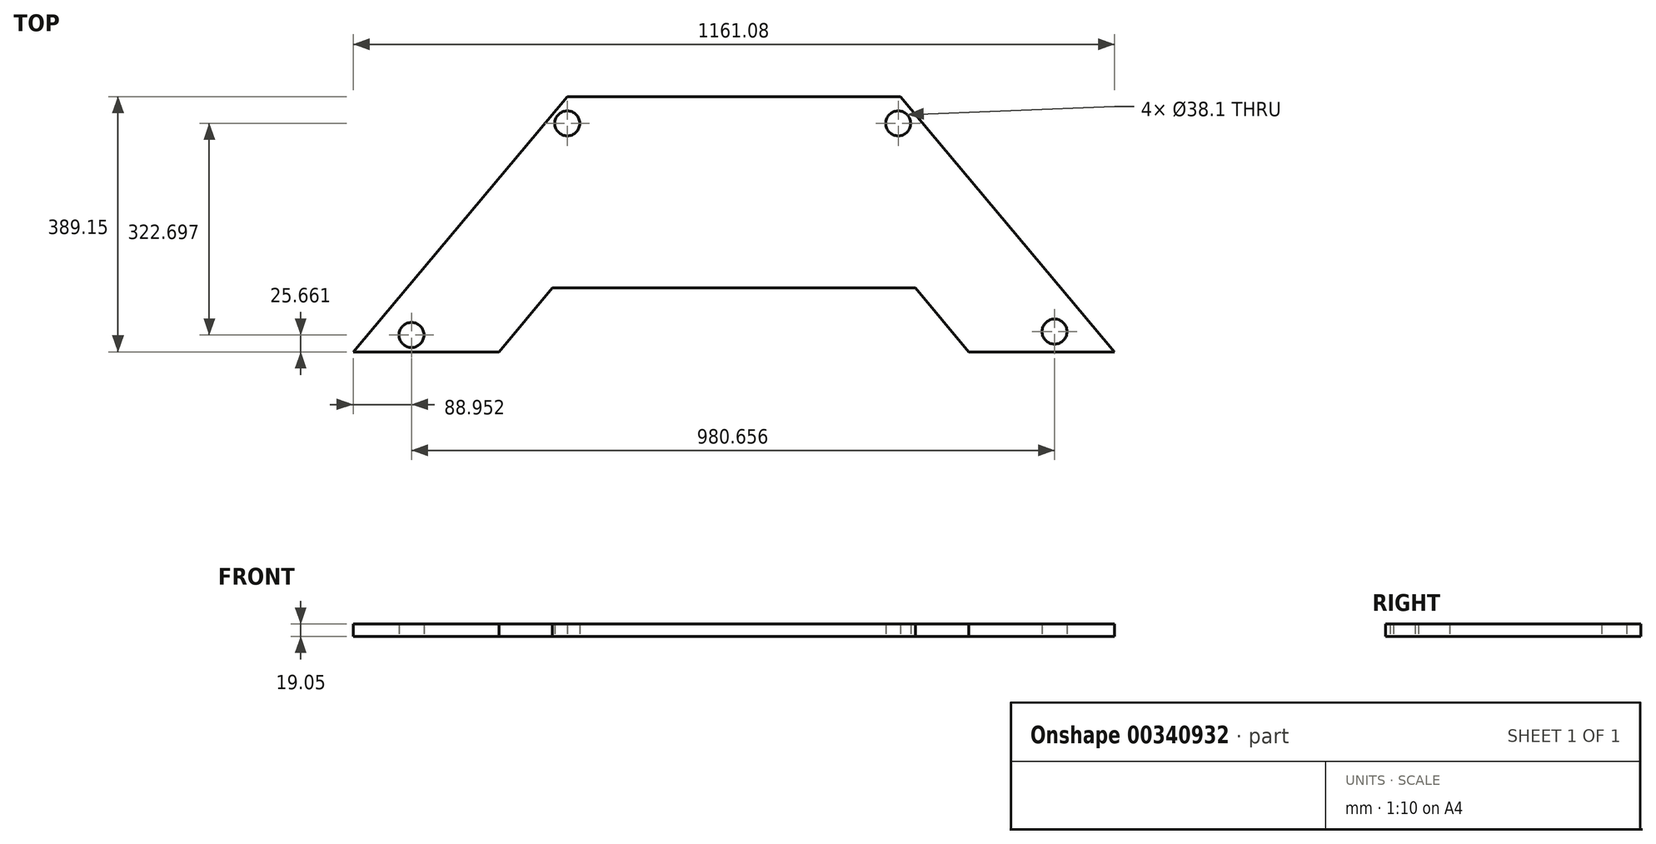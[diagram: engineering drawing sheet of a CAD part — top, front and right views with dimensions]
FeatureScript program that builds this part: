
annotation { "Feature Type Name" : "Feature", "Feature Type Description" : "" }
export const myFeature = defineFeature(function(context is Context, id is Id, definition is map)
    precondition{}
    {
        {
            var Q0;
            Q0=qCreatedBy(makeId("Top.planeOp"),FACE);
            var sketch = newSketch(context, id + "F0", { "sketchPlane" : qUnion([Q0])});
            skLineSegment(sketch, "E0", {"start": v(253.1, 0) * mm, "end": v(-254.9, 0) * mm});
            skLineSegment(sketch, "E1", {"start": v(-254.9, 0) * mm, "end": v(-581.43, -389.15) * mm});
            skLineSegment(sketch, "E2", {"start": v(253.1, 0) * mm, "end": v(579.65, -389.15) * mm});
            skLineSegment(sketch, "E3", {"start": v(-581.43, -389.15) * mm, "end": v(-359.18, -389.15) * mm});
            skLineSegment(sketch, "E4", {"start": v(579.65, -389.15) * mm, "end": v(357.4, -389.15) * mm});
            skLineSegment(sketch, "E5", {"start": v(-359.18, -389.15) * mm, "end": v(-277.54, -291.86) * mm});
            skLineSegment(sketch, "E6", {"start": v(357.4, -389.15) * mm, "end": v(275.76, -291.86) * mm});
            skLineSegment(sketch, "E7", {"start": v(-277.54, -291.86) * mm, "end": v(275.76, -291.86) * mm});
            skCircle(sketch, "E8", {"center": v(-254.9, -40.8) * mm, "radius": 19.05 * mm});
            skCircle(sketch, "E9", {"center": v(249.82, -40.8) * mm, "radius": 19.05 * mm});
            skCircle(sketch, "E10", {"center": v(-492.48, -363.49) * mm, "radius": 19.05 * mm});
            skCircle(sketch, "E11", {"center": v(488.18, -358.25) * mm, "radius": 19.05 * mm});
            skSolve(sketch);
        }
        {
            var Q0;
            Q0=makeQuery(id+"F0.imprint","IMPRINT",FACE,{"disambiguationData":[TD([[makeQuery(id+"F0.imprint","IMPRINT",EDGE,{"derivedFrom":sQuery(id+"F0.wireOp",EDGE,"E0")}),1.0]])]});
            extrude(context, id + "F1", {"entities" : qUnion([Q0]), "depth" : 19.05 * mm});
        }
        {
            var Q0;
            Q0=makeQuery(id+"F1.opExtrude","CAP_FACE",FACE,{"disambiguationData":[OSD([sQuery(id+"F0.wireOp",EDGE,"E0"),sQuery(id+"F0.wireOp",EDGE,"E1"),sQuery(id+"F0.wireOp",EDGE,"E2"),sQuery(id+"F0.wireOp",EDGE,"E3"),sQuery(id+"F0.wireOp",EDGE,"E4"),sQuery(id+"F0.wireOp",EDGE,"E5"),sQuery(id+"F0.wireOp",EDGE,"E6"),sQuery(id+"F0.wireOp",EDGE,"E7"),sQuery(id+"F0.wireOp",EDGE,"E8"),sQuery(id+"F0.wireOp",EDGE,"E9"),sQuery(id+"F0.wireOp",EDGE,"E10"),sQuery(id+"F0.wireOp",EDGE,"E11")])],"isStart":false});
            var sketch = newSketch(context, id + "F2", { "sketchPlane" : qUnion([Q0])});
            skSolve(sketch);
        }
        {
            var Q0;
            Q0=makeQuery(id+"F1.opExtrude","CAP_FACE",FACE,{"disambiguationData":[OSD([sQuery(id+"F0.wireOp",EDGE,"E0"),sQuery(id+"F0.wireOp",EDGE,"E1"),sQuery(id+"F0.wireOp",EDGE,"E2"),sQuery(id+"F0.wireOp",EDGE,"E3"),sQuery(id+"F0.wireOp",EDGE,"E4"),sQuery(id+"F0.wireOp",EDGE,"E5"),sQuery(id+"F0.wireOp",EDGE,"E6"),sQuery(id+"F0.wireOp",EDGE,"E7"),sQuery(id+"F0.wireOp",EDGE,"E8"),sQuery(id+"F0.wireOp",EDGE,"E9"),sQuery(id+"F0.wireOp",EDGE,"E10"),sQuery(id+"F0.wireOp",EDGE,"E11")])],"isStart":true});
            var sketch = newSketch(context, id + "F3", { "sketchPlane" : qUnion([Q0])});
            skCircle(sketch, "E12", {"center": v(488.18, 358.25) * mm, "radius": 19.05 * mm});
            skCircle(sketch, "E13", {"center": v(249.82, 40.8) * mm, "radius": 19.05 * mm});
            skCircle(sketch, "E14", {"center": v(-254.9, 40.8) * mm, "radius": 19.05 * mm});
            skCircle(sketch, "E15", {"center": v(-492.48, 363.49) * mm, "radius": 19.05 * mm});
            skSolve(sketch);
        }
        {
            var Q0;
            Q0=sQuery(id+"F3.wireOp",EDGE,"E15");
            var Q1;
            Q1=sQuery(id+"F3.wireOp",EDGE,"E14");
            var Q2;
            Q2=sQuery(id+"F3.wireOp",EDGE,"E13");
            var Q3;
            Q3=sQuery(id+"F3.wireOp",EDGE,"E12");
            extrude(context, id + "F4", {"bodyType" : ToolBodyType.SURFACE, "surfaceEntities" : qUnion([Q0, Q1, Q2, Q3]), "depth" : 660.4 * mm});
        }
    });
